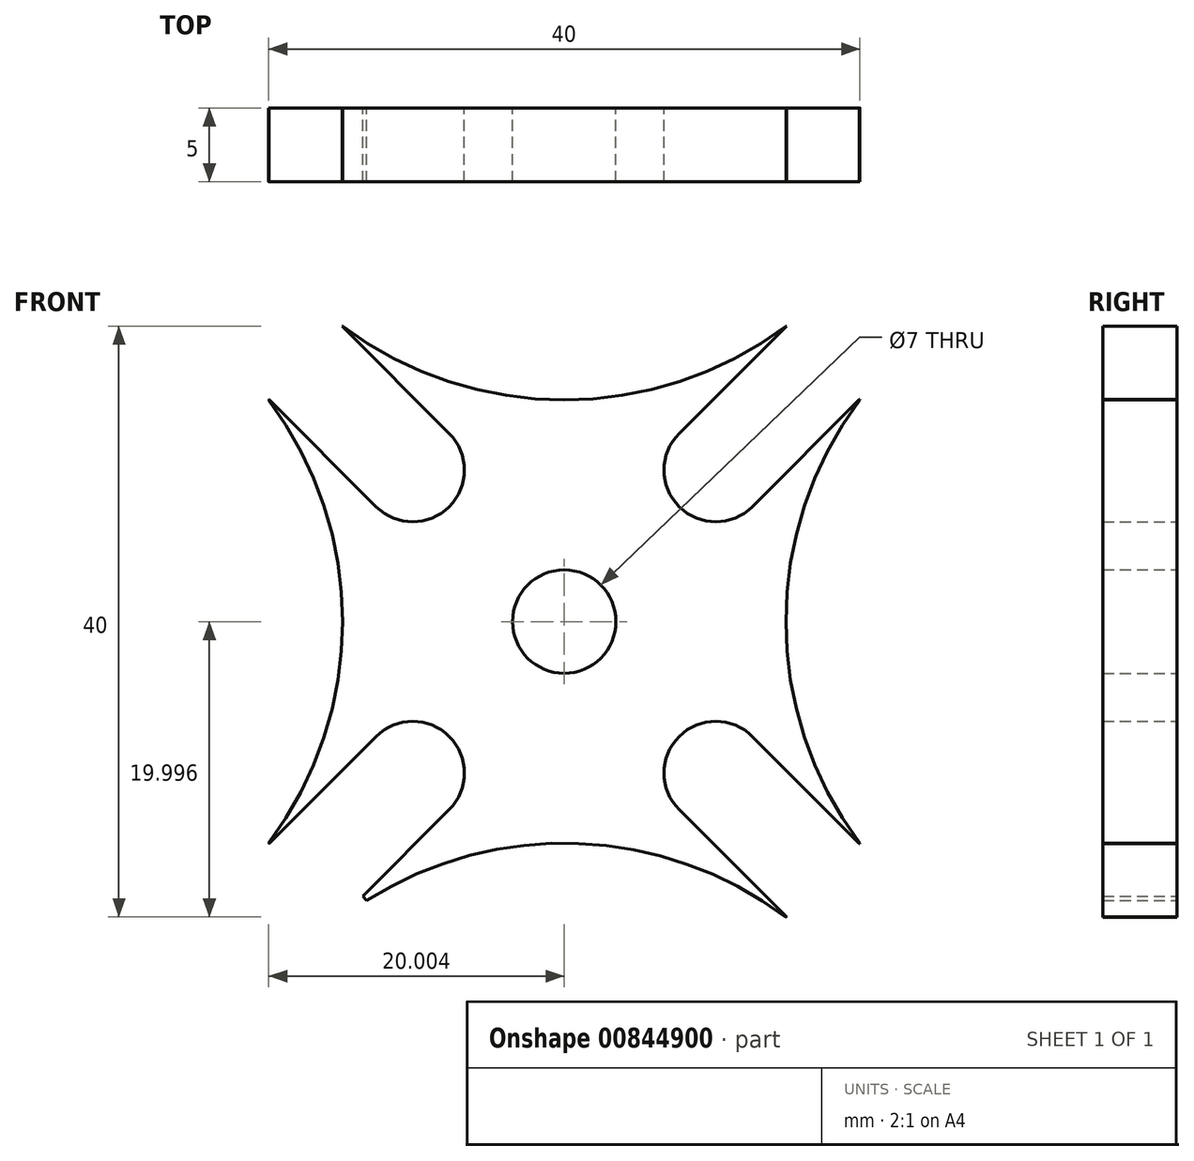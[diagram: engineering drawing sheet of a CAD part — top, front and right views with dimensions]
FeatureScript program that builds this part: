
annotation { "Feature Type Name" : "Feature", "Feature Type Description" : "" }
export const myFeature = defineFeature(function(context is Context, id is Id, definition is map)
    precondition{}
    {
        {
            var Q0;
            Q0=qCreatedBy(makeId("Front.planeOp"),FACE);
            var sketch = newSketch(context, id + "F0", { "sketchPlane" : qUnion([Q0])});
            skArc(sketch, "E0", {"start": v(-28.08, 24.95) * mm, "mid": v(-43.08, 29.95) * mm, "end": v(-58.08, 24.95) * mm});
            skArc(sketch, "E1.1.0", {"start": v(-23.08, 59.95) * mm, "mid": v(-28.08, 44.95) * mm, "end": v(-23.08, 29.95) * mm});
            skArc(sketch, "E1.2.0", {"start": v(-58.08, 64.95) * mm, "mid": v(-43.08, 59.95) * mm, "end": v(-28.08, 64.95) * mm});
            skArc(sketch, "E1.3.0", {"start": v(-63.08, 29.95) * mm, "mid": v(-58.08, 44.95) * mm, "end": v(-63.08, 59.95) * mm});
            skPoint(sketch, "E1.center", {"position": v(-43.08, 44.95) * mm});
            skLineSegment(sketch, "E2", {"start": v(-63.05, 29.92) * mm, "end": v(-48.03, 44.95) * mm});
            skLineSegment(sketch, "E3", {"start": v(-63.05, 59.98) * mm, "end": v(-48.03, 44.95) * mm});
            skLineSegment(sketch, "E4", {"start": v(-23.1, 29.92) * mm, "end": v(-38.13, 44.95) * mm});
            skLineSegment(sketch, "E5", {"start": v(-23.1, 59.98) * mm, "end": v(-38.13, 44.95) * mm});
            skArc(sketch, "E6", {"start": v(-50.85, 32.22) * mm, "mid": v(-50.85, 37.17) * mm, "end": v(-55.8, 37.17) * mm});
            skArc(sketch, "E7", {"start": v(-55.8, 52.72) * mm, "mid": v(-50.85, 52.72) * mm, "end": v(-50.85, 57.67) * mm});
            skArc(sketch, "E8", {"start": v(-35.3, 57.67) * mm, "mid": v(-35.3, 52.72) * mm, "end": v(-30.35, 52.72) * mm});
            skArc(sketch, "E9", {"start": v(-30.35, 37.17) * mm, "mid": v(-35.3, 37.17) * mm, "end": v(-35.3, 32.22) * mm});
            skCircle(sketch, "E10", {"center": v(-43.08, 44.95) * mm, "radius": 3.5 * mm});
            skArc(sketch, "E11", {"start": v(-38.18, 35.1) * mm, "mid": v(-35.3, 37.17) * mm, "end": v(-33.23, 40.05) * mm, "construction": true});
            skLineSegment(sketch, "E12", {"start": v(-43.08, 44.95) * mm, "end": v(-45.55, 42.47) * mm, "construction": true});
            skCircle(sketch, "E13", {"center": v(-60.75, 27.27) * mm, "radius": 2.5 * mm});
            skArc(sketch, "E14", {"start": v(-28.08, 24.95) * mm, "mid": v(-43.08, 69.95) * mm, "end": v(-58.08, 24.95) * mm});
            skLineSegment(sketch, "E15", {"start": v(-58.85, 28.89) * mm, "end": v(-56.45, 26.07) * mm});
            skLineSegment(sketch, "E16", {"start": v(-60.75, 27.27) * mm, "end": v(-59.2, 25.3) * mm, "construction": true});
            skLineSegment(sketch, "E17.trimOffspring", {"start": v(-43.08, 40) * mm, "end": v(-58.1, 24.97) * mm});
            skLineSegment(sketch, "E18.trimOffspring", {"start": v(-43.08, 49.9) * mm, "end": v(-58.1, 64.92) * mm});
            skLineSegment(sketch, "E19.trimOffspring", {"start": v(-43.08, 40) * mm, "end": v(-28.05, 24.97) * mm});
            skLineSegment(sketch, "E20.trimOffspring", {"start": v(-43.08, 49.9) * mm, "end": v(-28.05, 64.92) * mm});
            skLineSegment(sketch, "E21.trimOffspring", {"start": v(-50.85, 37.17) * mm, "end": v(-60.75, 27.27) * mm, "construction": true});
            skArc(sketch, "E22.trimOffspring", {"start": v(-50.85, 37.17) * mm, "mid": v(-49.5, 36.02) * mm, "end": v(-47.97, 35.1) * mm, "construction": true});
            skArc(sketch, "E23.trimOffspring", {"start": v(-47.97, 54.8) * mm, "mid": v(-50.85, 52.72) * mm, "end": v(-52.92, 49.85) * mm, "construction": true});
            skArc(sketch, "E24.trimOffspring", {"start": v(-33.23, 49.85) * mm, "mid": v(-34.15, 51.37) * mm, "end": v(-35.3, 52.72) * mm, "construction": true});
            skSolve(sketch);
        }
        {
            var Q0;
            {var subQ1=sQuery(id+"F0.wireOp",EDGE,"E0");var subQ5=sQuery(id+"F0.wireOp",EDGE,"E14");var subQ6=makeQuery(id+"F0.imprint","INTERSECT",VERTEX,{"disambiguationData":[OD(0.0)],"derivedFrom":[subQ1,subQ5]});Q0=makeQuery(id+"F0.imprint","IMPRINT",FACE,{"disambiguationData":[TD([[makeQuery(id+"F0.imprint","IMPRINT",EDGE,{"disambiguationData":[TD([[subQ6,-1.0]])],"derivedFrom":subQ1}),-1.0]])]});}
            var Q1;
            {var subQ1=sQuery(id+"F0.wireOp",EDGE,"E6");Q1=makeQuery(id+"F0.imprint","IMPRINT",FACE,{"disambiguationData":[TD([[makeQuery(id+"F0.imprint","IMPRINT",EDGE,{"derivedFrom":subQ1}),-1.0]])]});}
            var Q2;
            {var subQ8=sQuery(id+"F0.wireOp",EDGE,"E1.1.0");Q2=makeQuery(id+"F0.imprint","IMPRINT",FACE,{"disambiguationData":[TD([[makeQuery(id+"F0.imprint","IMPRINT",EDGE,{"derivedFrom":subQ8}),-1.0]])]});}
            var Q3;
            {var subQ8=sQuery(id+"F0.wireOp",EDGE,"E1.3.0");Q3=makeQuery(id+"F0.imprint","IMPRINT",FACE,{"disambiguationData":[TD([[makeQuery(id+"F0.imprint","IMPRINT",EDGE,{"derivedFrom":subQ8}),-1.0]])]});}
            var Q4;
            {var subQ1=sQuery(id+"F0.wireOp",EDGE,"E1.2.0");Q4=makeQuery(id+"F0.imprint","IMPRINT",FACE,{"disambiguationData":[TD([[makeQuery(id+"F0.imprint","IMPRINT",EDGE,{"derivedFrom":subQ1}),-1.0]])]});}
            extrude(context, id + "F1", {"entities" : qUnion([Q0, Q1, Q2, Q3, Q4]), "depth" : 5 * mm, "offsetDistance" : 25 * mm});
        }
    });
